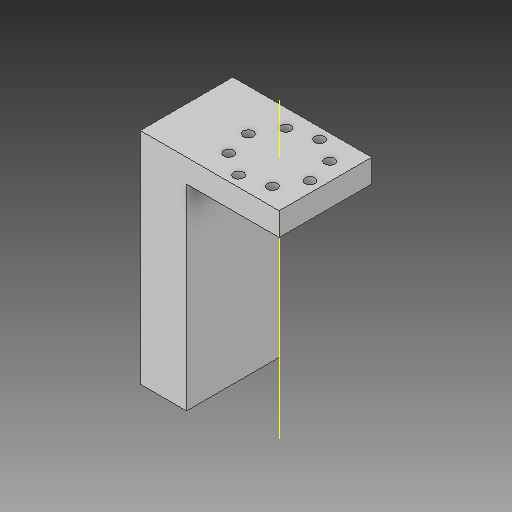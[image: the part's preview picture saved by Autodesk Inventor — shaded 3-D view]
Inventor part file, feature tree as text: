
AUTODESK INVENTOR PART (.ipt)
format: ipt  version: 2019 (Build 230136000, 136)  size: 130,560 bytes
history: native  units: in
note: dims shown in document units (in); Inventor stores cm internally (conversion verified against a paired STEP export)
features: sketch x2, extrude x1, hole x1, other x1
ambient origin geometry x8: Origin, YZ Plane, XZ Plane, XY Plane, X Axis, Y Axis, Z Axis, Center Point
bodies: Body1 (feature_tree)
feature tree (5):
  extrude  "Extrusion3"  Depth=0.25in
  hole  "Hole2"  [1 undecoded]
  other  "Work Axis1"
  sketch  "Sketch4"  dims[d25=2.371in d26=0.25in]
  sketch  "Sketch5"  dims[d27=1.0in d28=0.5in d29=1.0in d30=0.0in d34=3.1496in d36=360.0deg d38=0.107in d39=0.75in d40=0.375in d41=0.25in d42=0.5635in d43=1.0in d44=0.8108in d45=0.385in d46=0.5in d47=0.5in]
note: 1 required parameter value undecoded (feature->parameter linkage not recoverable at this tier; creation-order binding heuristic only, values carry confidence <= 0.55)
